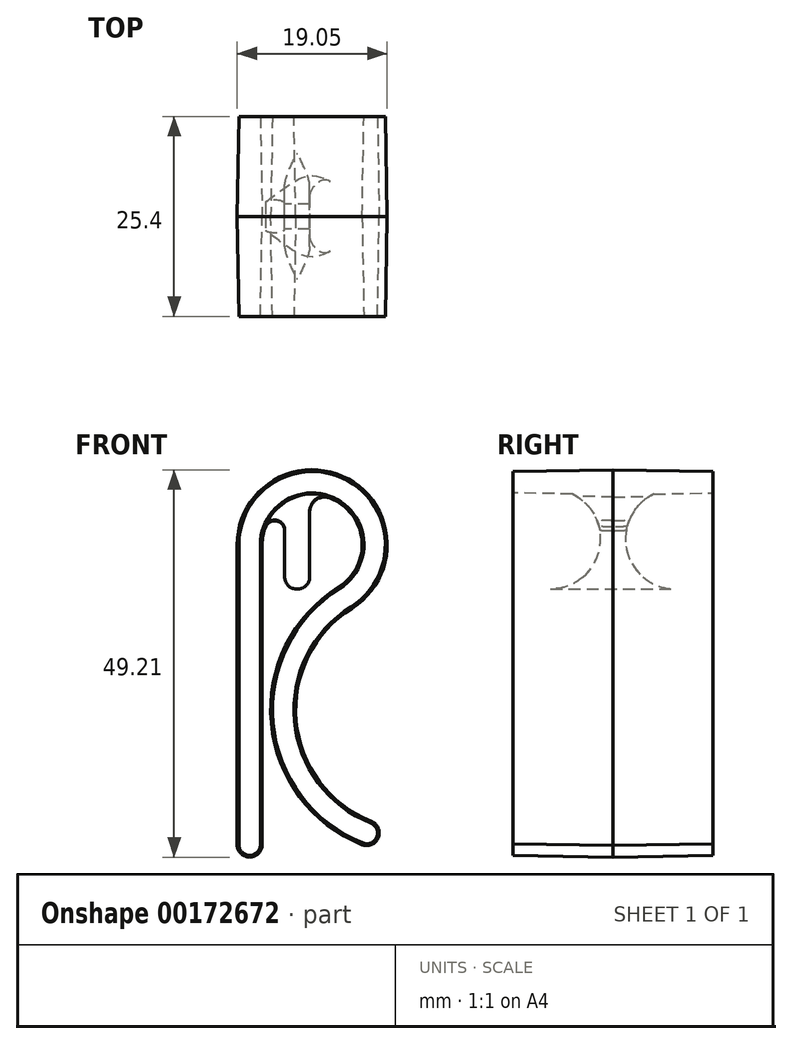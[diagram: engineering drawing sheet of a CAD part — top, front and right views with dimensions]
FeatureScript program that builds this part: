
annotation { "Feature Type Name" : "Feature", "Feature Type Description" : "" }
export const myFeature = defineFeature(function(context is Context, id is Id, definition is map)
    precondition{}
    {
        {
            var Q0;
            Q0=qCreatedBy(makeId("Front.planeOp"),FACE);
            var sketch = newSketch(context, id + "F0", { "sketchPlane" : qUnion([Q0])});
            skLineSegment(sketch, "E0", {"start": v(0, 0) * mm, "end": v(0, 38.1) * mm});
            skLineSegment(sketch, "E1", {"start": v(3.18, 0) * mm, "end": v(3.18, 38.1) * mm});
            skArc(sketch, "E2", {"start": v(12.9, 32.72) * mm, "mid": v(12.6, 43.66) * mm, "end": v(3.18, 38.1) * mm});
            skArc(sketch, "E3", {"start": v(12.9, 32.72) * mm, "mid": v(4.33, 15.44) * mm, "end": v(15.88, 0) * mm});
            skLineSegment(sketch, "E4", {"start": v(15.88, 0) * mm, "end": v(15.88, 41.76) * mm, "construction": true});
            skArc(sketch, "E5.0", {"start": v(14.58, 30.03) * mm, "mid": v(14.14, 46.43) * mm, "end": v(0, 38.1) * mm});
            skArc(sketch, "E6.0", {"start": v(14.58, 30.03) * mm, "mid": v(7.5, 15.73) * mm, "end": v(17.05, 2.95) * mm});
            skLineSegment(sketch, "E7", {"start": v(0, 0) * mm, "end": v(3.18, 0) * mm, "construction": true});
            skArc(sketch, "E8", {"start": v(0, 0) * mm, "mid": v(1.59, -1.59) * mm, "end": v(3.18, 0) * mm});
            skLineSegment(sketch, "E9", {"start": v(22.67, 17.11) * mm, "end": v(15.88, 0) * mm, "construction": true});
            skArc(sketch, "E10", {"start": v(15.88, 0) * mm, "mid": v(17.94, 0.89) * mm, "end": v(17.05, 2.95) * mm});
            skSolve(sketch);
        }
        {
            var Q0;
            Q0 = qSketchRegion(id + "F0", true);
            extrude(context, id + "F1", {"entities" : qUnion([Q0]), "depth" : 12.7 * mm, "hasDraft" : true, "draftAngle" : 1 * degree, "draftPullDirection" : true, "hasSecondDirection" : true, "secondDirectionOppositeDirection" : true, "secondDirectionDepth" : 12.7 * mm, "hasSecondDirectionDraft" : true, "secondDirectionDraftAngle" : 1 * degree, "secondDirectionDraftPullDirection" : true});
        }
        {
            var Q0;
            Q0=qCreatedBy(makeId("Right.planeOp"),FACE);
            cPlane(context, id + "F2", {"entities" : qUnion([Q0]), "cplaneType" : CPlaneType.OFFSET, "offset" : 7.62 * mm, "width" : 152.4 * mm, "height" : 152.4 * mm});
        }
        {
            var Q0;
            Q0=qCreatedBy(id+"F2.planeOp",FACE);
            var sketch = newSketch(context, id + "F3", { "sketchPlane" : qUnion([Q0])});
            skLineSegment(sketch, "E11.0", {"start": v(0, 30.03) * mm, "end": v(0, 47.62) * mm, "construction": true});
            skLineSegment(sketch, "E12.0", {"start": v(1.59, 30.03) * mm, "end": v(1.59, 47.62) * mm, "construction": true});
            skArc(sketch, "E13", {"start": v(7.94, 45.18) * mm, "mid": v(1.59, 38.83) * mm, "end": v(7.94, 32.48) * mm});
            skPoint(sketch, "E13.centerSnap0", {"position": v(1.59, 38.83) * mm});
            skLineSegment(sketch, "E14", {"start": v(7.94, 45.18) * mm, "end": v(0, 45.18) * mm});
            skLineSegment(sketch, "E15", {"start": v(7.94, 32.48) * mm, "end": v(0, 32.48) * mm});
            skLineSegment(sketch, "E16", {"start": v(1.59, 38.83) * mm, "end": v(7.94, 38.83) * mm, "construction": true});
            skArc(sketch, "E17.MirrorCS", {"start": v(-7.94, 45.18) * mm, "mid": v(-1.59, 38.83) * mm, "end": v(-7.94, 32.48) * mm});
            skLineSegment(sketch, "E18.MirrorCS", {"start": v(-7.94, 45.18) * mm, "end": v(0, 45.18) * mm});
            skLineSegment(sketch, "E19.MirrorCS", {"start": v(-7.94, 32.48) * mm, "end": v(0, 32.48) * mm});
            skSolve(sketch);
        }
        {
            var Q0;
            Q0=makeQuery(id+"F3.imprint","IMPRINT",FACE,{"disambiguationData":[TD([[makeQuery(id+"F3.imprint","IMPRINT",EDGE,{"derivedFrom":sQuery(id+"F3.wireOp",EDGE,"E13")}),-1.0]])]});
            extrude(context, id + "F4", {"entities" : qUnion([Q0]), "operationType" : NewBodyOperationType.ADD, "depth" : 1.59 * mm, "hasSecondDirection" : true, "secondDirectionOppositeDirection" : true, "secondDirectionDepth" : 1.59 * mm});
        }
        {
            var Q0;
            Q0=makeQuery(id+"F4.opExtrude","CAP_EDGE",EDGE,{"disambiguationData":[OSD([sQuery(id+"F3.wireOp",EDGE,"E15"),sQuery(id+"F3.wireOp",EDGE,"E19.MirrorCS")])],"isStart":false});
            var Q1;
            Q1=makeQuery(id+"F4.opExtrude","CAP_EDGE",EDGE,{"disambiguationData":[OSD([sQuery(id+"F3.wireOp",EDGE,"E15"),sQuery(id+"F3.wireOp",EDGE,"E19.MirrorCS")])],"isStart":true});
            fillet(context, id + "F5", {"entities" : qUnion([Q0, Q1]), "radius" : 1.52 * mm, "tangentPropagation" : true, "allowEdgeOverflow" : false});
        }
        {
            var Q0;
            Q0=makeQuery(id+"F4.boolean.opBoolean","INTERSECT",EDGE,{"derivedFrom":[makeQuery(id+"F1.split0.splitOp","SPLIT",FACE,{"derivedFrom":makeQuery(id+"F1.opExtrude","SWEPT_FACE",FACE,{"disambiguationData":[OSD([sQuery(id+"F0.wireOp",EDGE,"E2")])]})}),makeQuery(id+"F4.opExtrude","CAP_FACE",FACE,{"disambiguationData":[OSD([sQuery(id+"F3.wireOp",EDGE,"E13"),sQuery(id+"F3.wireOp",EDGE,"E14"),sQuery(id+"F3.wireOp",EDGE,"E15"),sQuery(id+"F3.wireOp",EDGE,"E17.MirrorCS"),sQuery(id+"F3.wireOp",EDGE,"E18.MirrorCS"),sQuery(id+"F3.wireOp",EDGE,"E19.MirrorCS")])],"isStart":false})]});
            fillet(context, id + "F6", {"entities" : qUnion([Q0]), "radius" : 1.9 * mm, "tangentPropagation" : true, "allowEdgeOverflow" : false});
        }
        {
            var Q0;
            Q0=makeQuery(id+"F4.boolean.opBoolean","INTERSECT",EDGE,{"derivedFrom":[makeQuery(id+"F1.split0.splitOp","SPLIT",FACE,{"derivedFrom":makeQuery(id+"F1.opExtrude","SWEPT_FACE",FACE,{"disambiguationData":[OSD([sQuery(id+"F0.wireOp",EDGE,"E2")])]})}),makeQuery(id+"F4.opExtrude","CAP_FACE",FACE,{"disambiguationData":[OSD([sQuery(id+"F3.wireOp",EDGE,"E13"),sQuery(id+"F3.wireOp",EDGE,"E14"),sQuery(id+"F3.wireOp",EDGE,"E15"),sQuery(id+"F3.wireOp",EDGE,"E17.MirrorCS"),sQuery(id+"F3.wireOp",EDGE,"E18.MirrorCS"),sQuery(id+"F3.wireOp",EDGE,"E19.MirrorCS")])],"isStart":true})]});
            fillet(context, id + "F7", {"entities" : qUnion([Q0]), "radius" : 1.27 * mm, "tangentPropagation" : true, "allowEdgeOverflow" : false});
        }
    });
